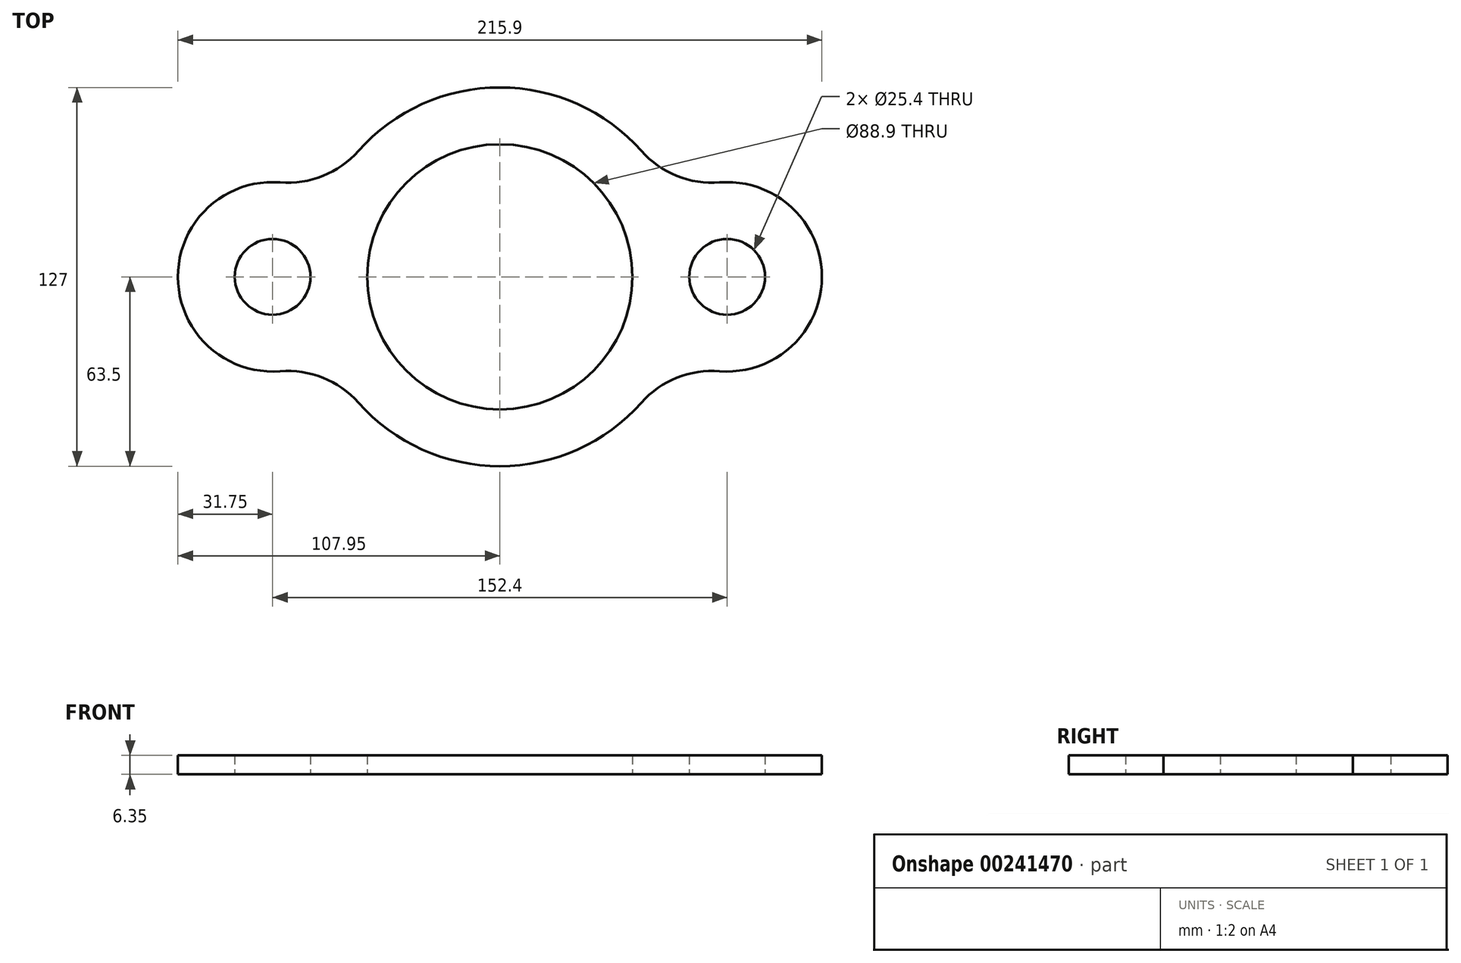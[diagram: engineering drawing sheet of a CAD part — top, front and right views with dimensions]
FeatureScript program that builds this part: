
annotation { "Feature Type Name" : "Feature", "Feature Type Description" : "" }
export const myFeature = defineFeature(function(context is Context, id is Id, definition is map)
    precondition{}
    {
        {
            var Q0;
            Q0=qCreatedBy(makeId("Top.planeOp"),FACE);
            var sketch = newSketch(context, id + "F0", { "sketchPlane" : qUnion([Q0])});
            skLineSegment(sketch, "E0", {"start": v(-63.5, 0) * mm, "end": v(-63.5, 0) * mm});
            skCircle(sketch, "E1", {"center": v(76.2, 0) * mm, "radius": 12.7 * mm});
            skCircle(sketch, "E2", {"center": v(-76.2, 0) * mm, "radius": 12.7 * mm});
            skCircle(sketch, "E3", {"center": v(0, 0) * mm, "radius": 44.45 * mm});
            skArc(sketch, "E4", {"start": v(-73.69, 31.65) * mm, "mid": v(-107.95, 0) * mm, "end": v(-73.69, -31.65) * mm});
            skArc(sketch, "E5", {"start": v(73.69, -31.65) * mm, "mid": v(107.95, 0) * mm, "end": v(73.69, 31.65) * mm});
            skArc(sketch, "E6.trimOffspring", {"start": v(-47.45, -42.2) * mm, "mid": v(0, -63.5) * mm, "end": v(47.45, -42.2) * mm});
            skArc(sketch, "E7.trimOffspring", {"start": v(47.45, 42.2) * mm, "mid": v(0, 63.5) * mm, "end": v(-47.45, 42.2) * mm});
            skPoint(sketch, "E8.visualSharp", {"position": v(-57.94, 25.98) * mm});
            skArc(sketch, "E8.filletArc", {"start": v(-73.69, 31.65) * mm, "mid": v(-59.33, 33.84) * mm, "end": v(-47.45, 42.2) * mm});
            skPoint(sketch, "E9.visualSharp", {"position": v(-57.94, -25.98) * mm});
            skArc(sketch, "E9.filletArc", {"start": v(-47.45, -42.2) * mm, "mid": v(-59.33, -33.84) * mm, "end": v(-73.69, -31.65) * mm});
            skPoint(sketch, "E10.visualSharp", {"position": v(57.94, -25.98) * mm});
            skArc(sketch, "E10.filletArc", {"start": v(73.69, -31.65) * mm, "mid": v(59.33, -33.84) * mm, "end": v(47.45, -42.2) * mm});
            skPoint(sketch, "E11.visualSharp", {"position": v(57.94, 25.98) * mm});
            skArc(sketch, "E11.filletArc", {"start": v(47.45, 42.2) * mm, "mid": v(59.33, 33.84) * mm, "end": v(73.69, 31.65) * mm});
            skSolve(sketch);
        }
        {
            var Q0;
            Q0=makeQuery(id+"F0.imprint","IMPRINT",FACE,{"disambiguationData":[TD([[makeQuery(id+"F0.imprint","IMPRINT",EDGE,{"derivedFrom":sQuery(id+"F0.wireOp",EDGE,"E1")}),-1.0]])]});
            extrude(context, id + "F1", {"entities" : qUnion([Q0]), "depth" : 6.35 * mm});
        }
    });
